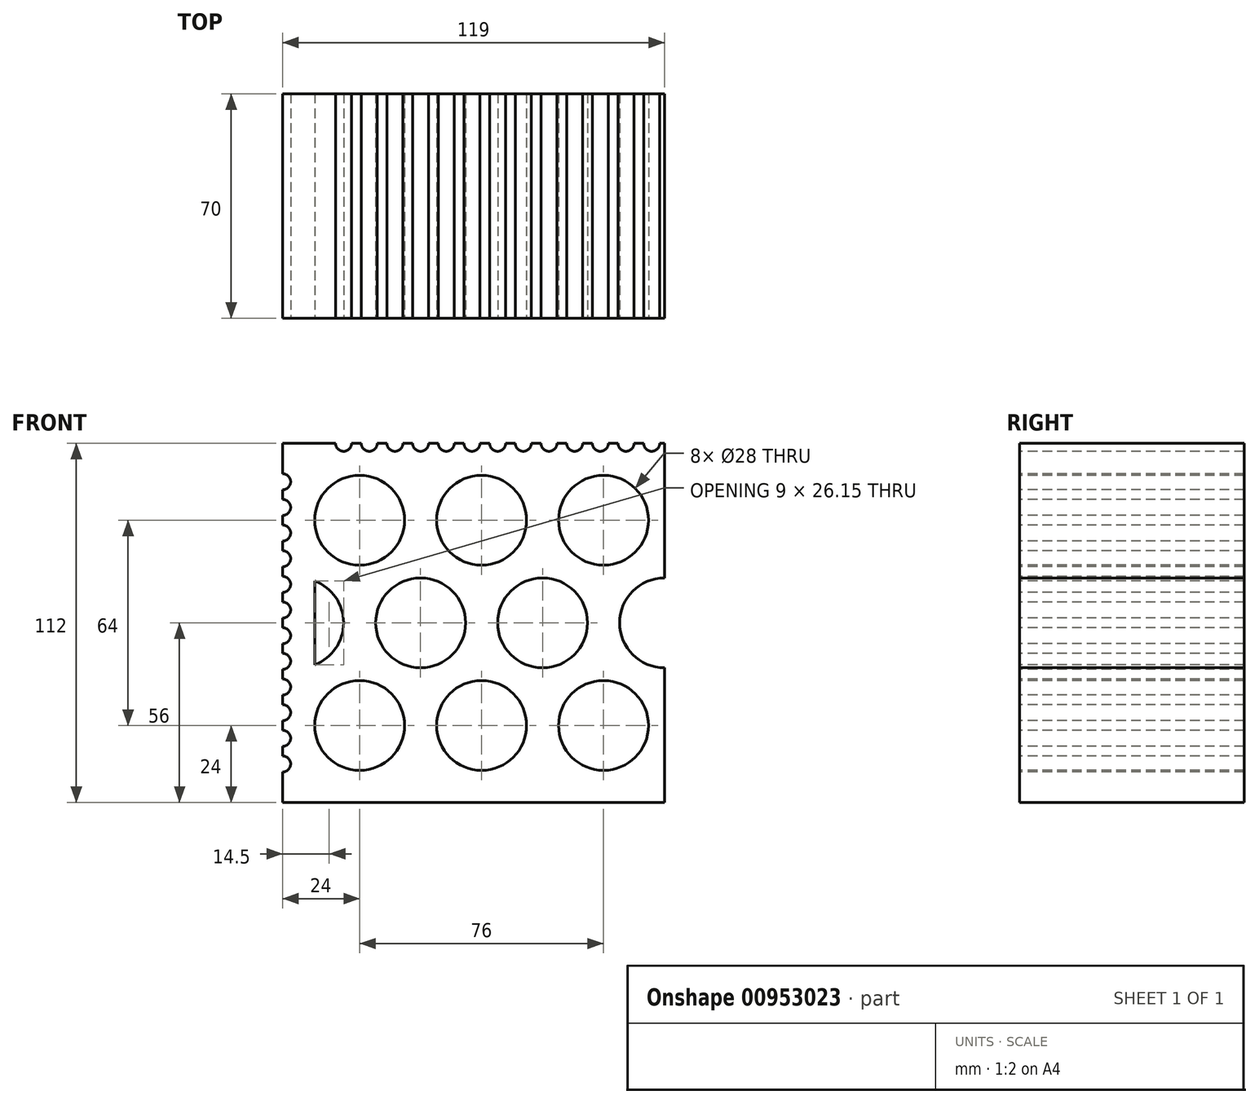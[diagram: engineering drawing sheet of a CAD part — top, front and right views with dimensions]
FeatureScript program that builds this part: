
annotation { "Feature Type Name" : "Feature", "Feature Type Description" : "" }
export const myFeature = defineFeature(function(context is Context, id is Id, definition is map)
    precondition{}
    {
        {
            var Q0;
            Q0=qCreatedBy(makeId("Front.planeOp"),FACE);
            var sketch = newSketch(context, id + "F0", { "sketchPlane" : qUnion([Q0])});
            skLineSegment(sketch, "E0.bottom", {"start": v(-119, -56) * mm, "end": v(0, -56) * mm});
            skLineSegment(sketch, "E0.top", {"start": v(-119, 56) * mm, "end": v(0, 56) * mm});
            skLineSegment(sketch, "E0.left", {"start": v(-119, -56) * mm, "end": v(-119, 56) * mm});
            skCircle(sketch, "E1", {"center": v(-95, 32) * mm, "radius": 14 * mm});
            skCircle(sketch, "E2.1.0.0", {"center": v(-57, 32) * mm, "radius": 14 * mm});
            skCircle(sketch, "E2.2.0.0", {"center": v(-19, 32) * mm, "radius": 14 * mm});
            skLineSegment(sketch, "E2.direction1", {"start": v(-95, 32) * mm, "end": v(-57, 32) * mm, "construction": true});
            skLineSegment(sketch, "E3", {"start": v(-119, 0) * mm, "end": v(0, 0) * mm, "construction": true});
            skCircle(sketch, "E4.MirrorC", {"center": v(-95, -32) * mm, "radius": 14 * mm});
            skCircle(sketch, "E5.MirrorC", {"center": v(-57, -32) * mm, "radius": 14 * mm});
            skCircle(sketch, "E6.MirrorC", {"center": v(-19, -32) * mm, "radius": 14 * mm});
            skCircle(sketch, "E7.1.0.0", {"center": v(-76, 0) * mm, "radius": 14 * mm});
            skCircle(sketch, "E7.2.0.0", {"center": v(-38, 0) * mm, "radius": 14 * mm});
            skArc(sketch, "E7.3.0.0", {"start": v(0, 14) * mm, "mid": v(-14, 0) * mm, "end": v(0, -14) * mm});
            skLineSegment(sketch, "E7.direction1", {"start": v(-114, 0) * mm, "end": v(-76, 0) * mm, "construction": true});
            skLineSegment(sketch, "E8", {"start": v(-109, 13.08) * mm, "end": v(-109, -13.08) * mm});
            skArc(sketch, "E9.trimOffspring", {"start": v(-109, -13.08) * mm, "mid": v(-100, 0) * mm, "end": v(-109, 13.08) * mm});
            skLineSegment(sketch, "E10", {"start": v(0, 56) * mm, "end": v(0, -56) * mm});
            skLineSegment(sketch, "E11", {"start": v(-119, 56) * mm, "end": v(-102.5, 56) * mm});
            skLineSegment(sketch, "E12", {"start": v(-102.5, 56) * mm, "end": v(-97.5, 56) * mm});
            skLineSegment(sketch, "E13", {"start": v(-97.5, 56) * mm, "end": v(-94.5, 56) * mm});
            skArc(sketch, "E14", {"start": v(-102.5, 56) * mm, "mid": v(-100, 53.5) * mm, "end": v(-97.5, 56) * mm});
            skArc(sketch, "E15.1.0.0", {"start": v(-94.5, 56) * mm, "mid": v(-92, 53.5) * mm, "end": v(-89.5, 56) * mm});
            skLineSegment(sketch, "E15.1.0.1", {"start": v(-89.5, 56) * mm, "end": v(-86.5, 56) * mm});
            skArc(sketch, "E15.2.0.0", {"start": v(-86.5, 56) * mm, "mid": v(-84, 53.5) * mm, "end": v(-81.5, 56) * mm});
            skLineSegment(sketch, "E15.2.0.1", {"start": v(-81.5, 56) * mm, "end": v(-78.5, 56) * mm});
            skArc(sketch, "E15.3.0.0", {"start": v(-78.5, 56) * mm, "mid": v(-76, 53.5) * mm, "end": v(-73.5, 56) * mm});
            skLineSegment(sketch, "E15.3.0.1", {"start": v(-73.5, 56) * mm, "end": v(-70.5, 56) * mm});
            skArc(sketch, "E15.4.0.0", {"start": v(-70.5, 56) * mm, "mid": v(-68, 53.5) * mm, "end": v(-65.5, 56) * mm});
            skLineSegment(sketch, "E15.4.0.1", {"start": v(-65.5, 56) * mm, "end": v(-62.5, 56) * mm});
            skArc(sketch, "E15.5.0.0", {"start": v(-62.5, 56) * mm, "mid": v(-60, 53.5) * mm, "end": v(-57.5, 56) * mm});
            skLineSegment(sketch, "E15.5.0.1", {"start": v(-57.5, 56) * mm, "end": v(-54.5, 56) * mm});
            skArc(sketch, "E15.6.0.0", {"start": v(-54.5, 56) * mm, "mid": v(-52, 53.5) * mm, "end": v(-49.5, 56) * mm});
            skLineSegment(sketch, "E15.6.0.1", {"start": v(-49.5, 56) * mm, "end": v(-46.5, 56) * mm});
            skArc(sketch, "E15.7.0.0", {"start": v(-46.5, 56) * mm, "mid": v(-44, 53.5) * mm, "end": v(-41.5, 56) * mm});
            skLineSegment(sketch, "E15.7.0.1", {"start": v(-41.5, 56) * mm, "end": v(-38.5, 56) * mm});
            skArc(sketch, "E15.8.0.0", {"start": v(-38.5, 56) * mm, "mid": v(-36, 53.5) * mm, "end": v(-33.5, 56) * mm});
            skLineSegment(sketch, "E15.8.0.1", {"start": v(-33.5, 56) * mm, "end": v(-30.5, 56) * mm});
            skArc(sketch, "E15.9.0.0", {"start": v(-30.5, 56) * mm, "mid": v(-28, 53.5) * mm, "end": v(-25.5, 56) * mm});
            skLineSegment(sketch, "E15.9.0.1", {"start": v(-25.5, 56) * mm, "end": v(-22.5, 56) * mm});
            skArc(sketch, "E15.10.0.0", {"start": v(-22.5, 56) * mm, "mid": v(-20, 53.5) * mm, "end": v(-17.5, 56) * mm});
            skLineSegment(sketch, "E15.10.0.1", {"start": v(-17.5, 56) * mm, "end": v(-14.5, 56) * mm});
            skArc(sketch, "E15.11.0.0", {"start": v(-14.5, 56) * mm, "mid": v(-12, 53.5) * mm, "end": v(-9.5, 56) * mm});
            skLineSegment(sketch, "E15.11.0.1", {"start": v(-9.5, 56) * mm, "end": v(-6.5, 56) * mm});
            skArc(sketch, "E15.12.0.0", {"start": v(-6.5, 56) * mm, "mid": v(-4, 53.5) * mm, "end": v(-1.5, 56) * mm});
            skLineSegment(sketch, "E15.direction1", {"start": v(-102.5, 56) * mm, "end": v(-94.5, 56) * mm, "construction": true});
            skLineSegment(sketch, "E16.MirrorCS", {"start": v(-119, 38.5) * mm, "end": v(-119, 33.5) * mm});
            skLineSegment(sketch, "E17.MirrorCS", {"start": v(-119, 38.5) * mm, "end": v(-119, 30.5) * mm, "construction": true});
            skLineSegment(sketch, "E18.MirrorCS", {"start": v(-119, 22.5) * mm, "end": v(-119, 17.5) * mm});
            skLineSegment(sketch, "E19.MirrorCS", {"start": v(-119, -14.5) * mm, "end": v(-119, -17.5) * mm});
            skLineSegment(sketch, "E20.MirrorCS", {"start": v(-119, 33.5) * mm, "end": v(-119, 30.5) * mm});
            skLineSegment(sketch, "E21.MirrorCS", {"start": v(-119, 9.5) * mm, "end": v(-119, 6.5) * mm});
            skLineSegment(sketch, "E22.MirrorCS", {"start": v(-119, 6.5) * mm, "end": v(-119, 1.5) * mm});
            skLineSegment(sketch, "E23.MirrorCS", {"start": v(-119, 41.5) * mm, "end": v(-119, 38.5) * mm});
            skLineSegment(sketch, "E24.MirrorCS", {"start": v(-119, 1.5) * mm, "end": v(-119, -1.5) * mm});
            skLineSegment(sketch, "E25.MirrorCS", {"start": v(-119, -30.5) * mm, "end": v(-119, -33.5) * mm});
            skLineSegment(sketch, "E26.MirrorCS", {"start": v(-119, 30.5) * mm, "end": v(-119, 25.5) * mm});
            skLineSegment(sketch, "E27.MirrorCS", {"start": v(-119, -17.5) * mm, "end": v(-119, -22.5) * mm});
            skLineSegment(sketch, "E28.MirrorCS", {"start": v(-119, -1.5) * mm, "end": v(-119, -6.5) * mm});
            skLineSegment(sketch, "E29.MirrorCS", {"start": v(-119, 14.5) * mm, "end": v(-119, 9.5) * mm});
            skLineSegment(sketch, "E30.MirrorCS", {"start": v(-119, -9.5) * mm, "end": v(-119, -14.5) * mm});
            skLineSegment(sketch, "E31.MirrorCS", {"start": v(-119, 46.5) * mm, "end": v(-119, 41.5) * mm});
            skLineSegment(sketch, "E32.MirrorCS", {"start": v(-119, -25.5) * mm, "end": v(-119, -30.5) * mm});
            skLineSegment(sketch, "E33.MirrorCS", {"start": v(-119, -38.5) * mm, "end": v(-119, -41.5) * mm});
            skLineSegment(sketch, "E34.MirrorCS", {"start": v(-119, 17.5) * mm, "end": v(-119, 14.5) * mm});
            skLineSegment(sketch, "E35.MirrorCS", {"start": v(-119, -22.5) * mm, "end": v(-119, -25.5) * mm});
            skLineSegment(sketch, "E36.MirrorCS", {"start": v(-119, -6.5) * mm, "end": v(-119, -9.5) * mm});
            skLineSegment(sketch, "E37.MirrorCS", {"start": v(-119, 25.5) * mm, "end": v(-119, 22.5) * mm});
            skLineSegment(sketch, "E38.MirrorCS", {"start": v(-119, -33.5) * mm, "end": v(-119, -38.5) * mm});
            skLineSegment(sketch, "E39.MirrorCS", {"start": v(-119, -41.5) * mm, "end": v(-119, -46.5) * mm});
            skArc(sketch, "E40.MirrorCS", {"start": v(-119, 22.5) * mm, "mid": v(-116.5, 20) * mm, "end": v(-119, 17.5) * mm});
            skArc(sketch, "E41.MirrorCS", {"start": v(-119, 6.5) * mm, "mid": v(-116.5, 4) * mm, "end": v(-119, 1.5) * mm});
            skArc(sketch, "E42.MirrorCS", {"start": v(-119, -33.5) * mm, "mid": v(-116.5, -36) * mm, "end": v(-119, -38.5) * mm});
            skArc(sketch, "E43.MirrorCS", {"start": v(-119, -25.5) * mm, "mid": v(-116.5, -28) * mm, "end": v(-119, -30.5) * mm});
            skArc(sketch, "E44.MirrorCS", {"start": v(-119, 30.5) * mm, "mid": v(-116.5, 28) * mm, "end": v(-119, 25.5) * mm});
            skArc(sketch, "E45.MirrorCS", {"start": v(-119, -9.5) * mm, "mid": v(-116.5, -12) * mm, "end": v(-119, -14.5) * mm});
            skArc(sketch, "E46.MirrorCS", {"start": v(-119, -1.5) * mm, "mid": v(-116.5, -4) * mm, "end": v(-119, -6.5) * mm});
            skArc(sketch, "E47.MirrorCS", {"start": v(-119, 46.5) * mm, "mid": v(-116.5, 44) * mm, "end": v(-119, 41.5) * mm});
            skArc(sketch, "E48.MirrorCS", {"start": v(-119, 38.5) * mm, "mid": v(-116.5, 36) * mm, "end": v(-119, 33.5) * mm});
            skArc(sketch, "E49.MirrorCS", {"start": v(-119, -17.5) * mm, "mid": v(-116.5, -20) * mm, "end": v(-119, -22.5) * mm});
            skArc(sketch, "E50.MirrorCS", {"start": v(-119, 14.5) * mm, "mid": v(-116.5, 12) * mm, "end": v(-119, 9.5) * mm});
            skLineSegment(sketch, "E51.MirrorCS", {"start": v(-118.18, 18.4) * mm, "end": v(-118.18, 18.4) * mm});
            skArc(sketch, "E52.MirrorCS", {"start": v(-119, -41.5) * mm, "mid": v(-116.5, -44) * mm, "end": v(-119, -46.5) * mm});
            skLineSegment(sketch, "E53", {"start": v(0, 56) * mm, "end": v(0, -56) * mm, "construction": true});
            skLineSegment(sketch, "E54.12.0.1", {"start": v(-1.5, 56) * mm, "end": v(0, 56) * mm});
            skLineSegment(sketch, "E55.top", {"start": v(-119, 56) * mm, "end": v(-1.5, 56) * mm});
            skArc(sketch, "E56.3.0.0", {"start": v(0, 14) * mm, "mid": v(-9.9, 9.9) * mm, "end": v(-14, 0) * mm});
            skLineSegment(sketch, "E57", {"start": v(0, -14) * mm, "end": v(0, 14) * mm});
            skSolve(sketch);
        }
        {
            var Q0;
            {var subQ9=sQuery(id+"F0.wireOp",EDGE,"E7.3.0.0");Q0=makeQuery(id+"F0.imprint","IMPRINT",FACE,{"disambiguationData":[TD([[makeQuery(id+"F0.imprint","IMPRINT",EDGE,{"derivedFrom":subQ9}),-1.0]])]});}
            extrude(context, id + "F1", {"entities" : qUnion([Q0]), "oppositeDirection" : true, "depth" : 70 * mm, "offsetDistance" : 25 * mm});
        }
    });
